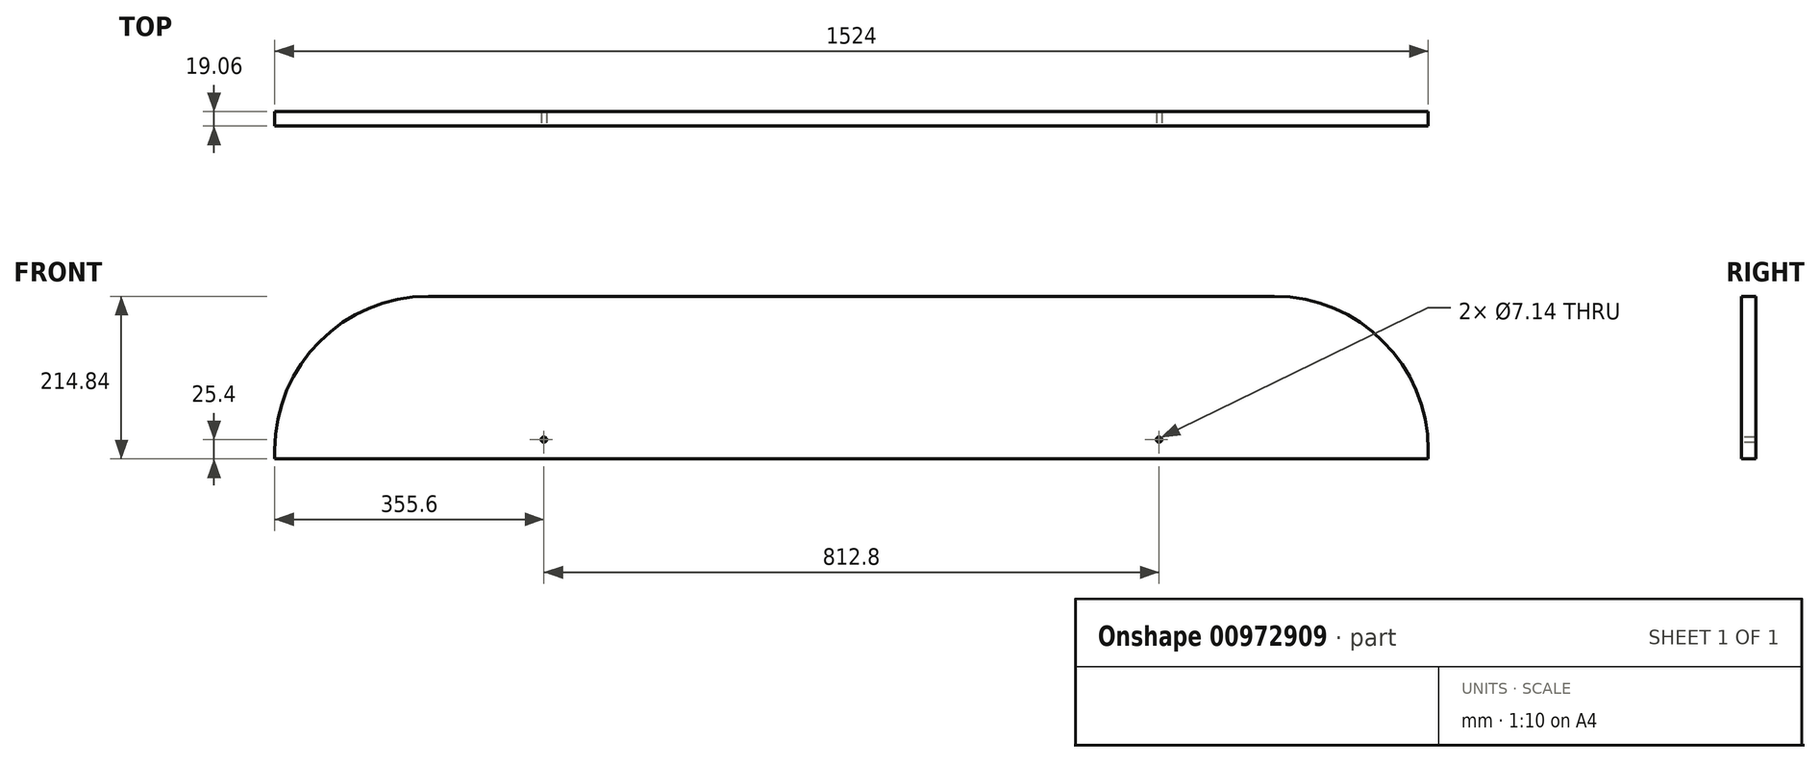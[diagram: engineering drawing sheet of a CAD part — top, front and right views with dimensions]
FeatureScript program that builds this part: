
annotation { "Feature Type Name" : "Feature", "Feature Type Description" : "" }
export const myFeature = defineFeature(function(context is Context, id is Id, definition is map)
    precondition{}
    {
        {
            var Q0;
            Q0=qCreatedBy(makeId("Front.planeOp"),FACE);
            var sketch = newSketch(context, id + "F0", { "sketchPlane" : qUnion([Q0])});
            skLineSegment(sketch, "E0.bottom", {"start": v(-762, 0) * mm, "end": v(762, 0) * mm});
            skLineSegment(sketch, "E0.top", {"start": v(-558.8, 214.84) * mm, "end": v(558.8, 214.84) * mm});
            skLineSegment(sketch, "E0.left", {"start": v(-762, 0) * mm, "end": v(-762, 11.64) * mm});
            skLineSegment(sketch, "E0.right", {"start": v(762, 0) * mm, "end": v(762, 11.64) * mm});
            skPoint(sketch, "E1.visualSharp", {"position": v(-762, 214.84) * mm});
            skArc(sketch, "E1.filletArc", {"start": v(-558.8, 214.84) * mm, "mid": v(-702.48, 155.33) * mm, "end": v(-762, 11.64) * mm});
            skPoint(sketch, "E2.visualSharp", {"position": v(762, 214.84) * mm});
            skArc(sketch, "E2.filletArc", {"start": v(762, 11.64) * mm, "mid": v(702.48, 155.33) * mm, "end": v(558.8, 214.84) * mm});
            skSolve(sketch);
        }
        {
            var Q0;
            Q0=makeQuery(id+"F0.imprint","IMPRINT",FACE,{"disambiguationData":[TD([[makeQuery(id+"F0.imprint","IMPRINT",EDGE,{"derivedFrom":sQuery(id+"F0.wireOp",EDGE,"E0.bottom")}),1.0]])]});
            extrude(context, id + "F1", {"entities" : qUnion([Q0]), "depth" : 9.52 * mm, "offsetDistance" : 25.4 * mm, "hasSecondDirection" : true, "secondDirectionOppositeDirection" : true, "secondDirectionDepth" : 9.52 * mm});
        }
        {
            var Q0;
            Q0=makeQuery(id+"F1.opExtrude","CAP_FACE",FACE,{"disambiguationData":[OSD([sQuery(id+"F0.wireOp",EDGE,"E0.bottom"),sQuery(id+"F0.wireOp",EDGE,"E0.top"),sQuery(id+"F0.wireOp",EDGE,"E0.left"),sQuery(id+"F0.wireOp",EDGE,"E0.right"),sQuery(id+"F0.wireOp",EDGE,"E1.filletArc"),sQuery(id+"F0.wireOp",EDGE,"E2.filletArc")])],"isStart":false});
            var sketch = newSketch(context, id + "F2", { "sketchPlane" : qUnion([Q0])});
            skPoint(sketch, "E3", {"position": v(-406.4, 25.4) * mm});
            skPoint(sketch, "E4.MirrorP", {"position": v(406.4, 25.4) * mm});
            skSolve(sketch);
        }
        {
            var Q0;
            Q0=sQuery(id+"F2.wireOp",VERTEX,"E3");
            var Q1;
            Q1=sQuery(id+"F2.wireOp",VERTEX,"E4.MirrorP");
            var Q2;
            Q2=makeQuery(id+"F1.opExtrude","SWEPT_BODY",BODY,{"disambiguationData":[OSD([sQuery(id+"F0.wireOp",EDGE,"E0.bottom"),sQuery(id+"F0.wireOp",EDGE,"E0.top"),sQuery(id+"F0.wireOp",EDGE,"E0.left"),sQuery(id+"F0.wireOp",EDGE,"E0.right"),sQuery(id+"F0.wireOp",EDGE,"E1.filletArc"),sQuery(id+"F0.wireOp",EDGE,"E2.filletArc")])]});
            hole(context, id + "F3", {"style" : HoleStyle.SIMPLE, "endStyle" : HoleEndStyle.THROUGH, "standardTappedOrClearance" : lookupTablePath({ "fit" : "Normal (ASME)", "standard" : "ANSI", "size" : "1/4", "type" : "Clearance" }), "standardBlindInLast" : lookupTablePath({ "fit" : "Normal", "standard" : "ANSI", "engagement" : "75%", "pitch" : "20 tpi", "size" : "1/4", "type" : "Clearance & tapped" }), "holeDiameter" : 7.14 * mm, "majorDiameter" : 6.35 * mm, "isTappedThrough" : true, "tappedDepth" : 12.7 * mm, "tapClearance" : 3, "locations" : qUnion([Q0, Q1]), "scope" : qUnion([Q2])});
        }
    });
